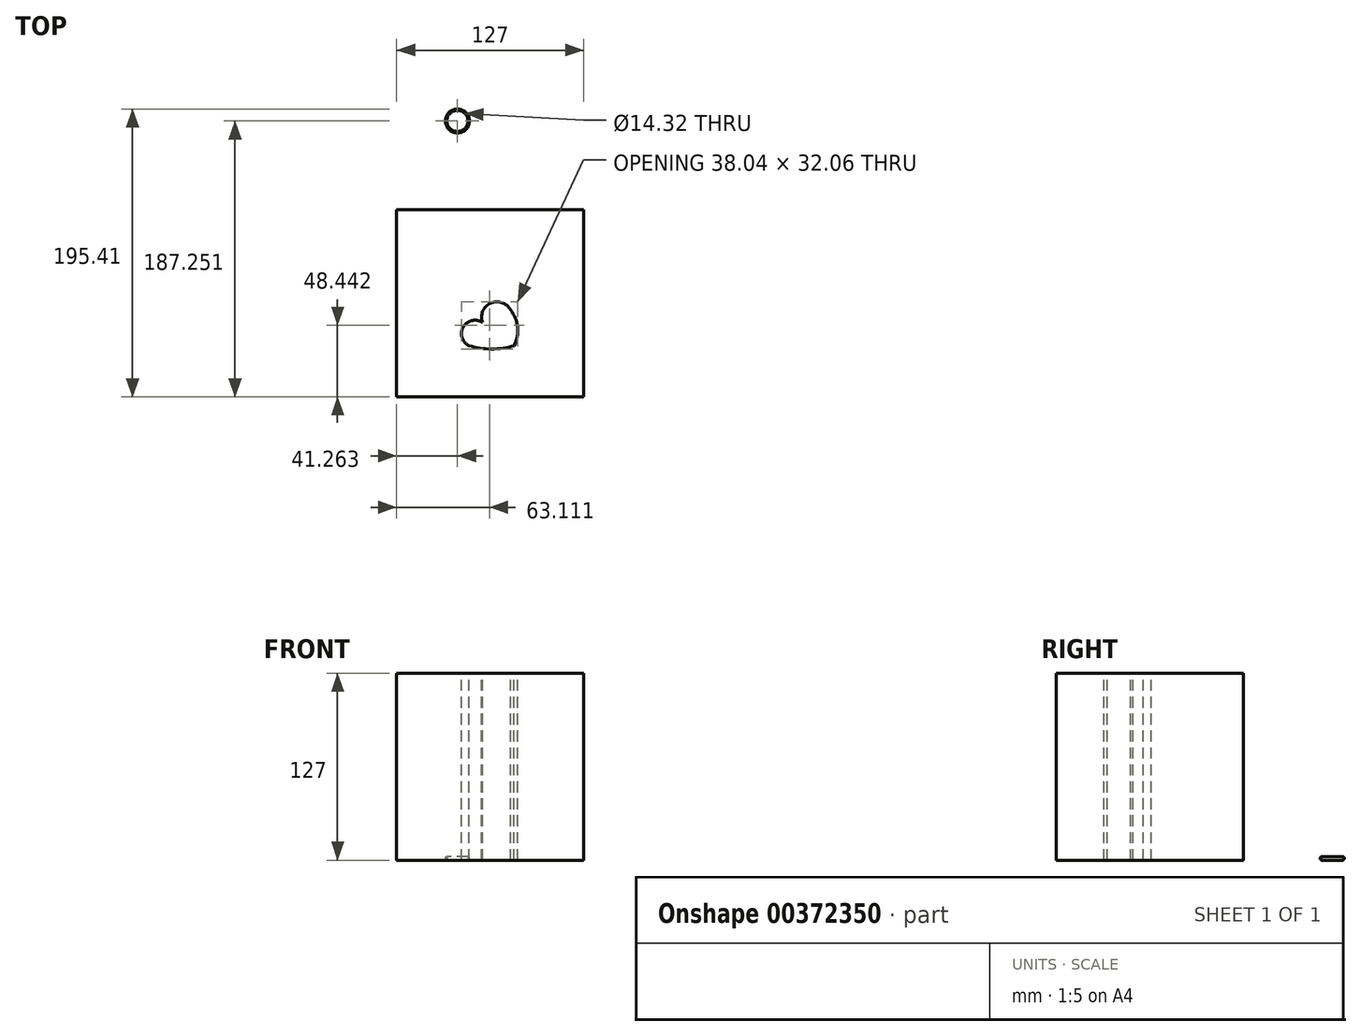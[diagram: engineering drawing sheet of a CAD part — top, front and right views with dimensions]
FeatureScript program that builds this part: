
annotation { "Feature Type Name" : "Feature", "Feature Type Description" : "" }
export const myFeature = defineFeature(function(context is Context, id is Id, definition is map)
    precondition{}
    {
        {
            var Q0;
            Q0=qCreatedBy(makeId("Top.planeOp"),FACE);
            var sketch = newSketch(context, id + "F0", { "sketchPlane" : qUnion([Q0])});
            skLineSegment(sketch, "E0.bottom", {"start": v(0, 0) * mm, "end": v(127, 0) * mm});
            skLineSegment(sketch, "E0.top", {"start": v(0, -127) * mm, "end": v(127, -127) * mm});
            skLineSegment(sketch, "E0.left", {"start": v(0, 0) * mm, "end": v(0, -127) * mm});
            skLineSegment(sketch, "E0.right", {"start": v(127, 0) * mm, "end": v(127, -127) * mm});
            skPoint(sketch, "E0.middle", {"position": v(63.5, -63.5) * mm});
            skSolve(sketch);
        }
        {
            var Q0;
            Q0=makeQuery(id+"F0.imprint","IMPRINT",FACE,{"disambiguationData":[TD([[makeQuery(id+"F0.imprint","IMPRINT",EDGE,{"derivedFrom":sQuery(id+"F0.wireOp",EDGE,"E0.bottom")}),-1.0]])]});
            extrude(context, id + "F1", {"entities" : qUnion([Q0]), "depth" : 127 * mm});
        }
        {
            var Q0;
            Q0=makeQuery(id+"F1.opExtrude","CAP_FACE",FACE,{"disambiguationData":[OSD([sQuery(id+"F0.wireOp",EDGE,"E0.bottom"),sQuery(id+"F0.wireOp",EDGE,"E0.top"),sQuery(id+"F0.wireOp",EDGE,"E0.left"),sQuery(id+"F0.wireOp",EDGE,"E0.right")])],"isStart":false});
            var sketch = newSketch(context, id + "F2", { "sketchPlane" : qUnion([Q0])});
            skArc(sketch, "E1", {"start": v(77.28, -67.94) * mm, "mid": v(63.78, -63.45) * mm, "end": v(58.25, -76.57) * mm});
            skArc(sketch, "E2", {"start": v(79.76, -92.34) * mm, "mid": v(82.03, -79.79) * mm, "end": v(77.28, -67.94) * mm});
            skArc(sketch, "E3", {"start": v(49.17, -92.34) * mm, "mid": v(64.46, -94.59) * mm, "end": v(79.76, -92.34) * mm});
            skArc(sketch, "E4", {"start": v(58.25, -76.57) * mm, "mid": v(45.25, -79.58) * mm, "end": v(49.17, -92.34) * mm});
            skSolve(sketch);
        }
        {
            var Q0;
            Q0 = qSketchRegion(id + "F2", true);
            extrude(context, id + "F3", {"entities" : qUnion([Q0]), "operationType" : NewBodyOperationType.REMOVE, "endBound" : BoundingType.THROUGH_ALL, "oppositeDirection" : true, "depth" : 25.4 * mm});
        }
        {
            var Q0;
            Q0=qCreatedBy(makeId("Top.planeOp"),FACE);
            var sketch = newSketch(context, id + "F4", { "sketchPlane" : qUnion([Q0])});
            skCircle(sketch, "E5", {"center": v(41.26, 60.25) * mm, "radius": 8.16 * mm});
            skCircle(sketch, "E6", {"center": v(41.26, 60.25) * mm, "radius": 7.16 * mm});
            skSolve(sketch);
        }
        {
            var Q0;
            Q0=makeQuery(id+"F4.imprint","IMPRINT",FACE,{"disambiguationData":[TD([[makeQuery(id+"F4.imprint","IMPRINT",EDGE,{"derivedFrom":sQuery(id+"F4.wireOp",EDGE,"E5")}),1.0]])]});
            extrude(context, id + "F5", {"entities" : qUnion([Q0]), "depth" : 2.54 * mm});
        }
        {
            var Q0;
            Q0=makeQuery(id+"F5.opExtrude","CAP_EDGE",EDGE,{"disambiguationData":[OSD([sQuery(id+"F4.wireOp",EDGE,"E5")])],"isStart":true});
            var Q1;
            Q1=makeQuery(id+"F5.opExtrude","CAP_EDGE",EDGE,{"disambiguationData":[OSD([sQuery(id+"F4.wireOp",EDGE,"E5")])],"isStart":false});
            fillet(context, id + "F6", {"entities" : qUnion([Q0, Q1]), "radius" : 1.3 * mm, "tangentPropagation" : true, "allowEdgeOverflow" : false});
        }
    });
